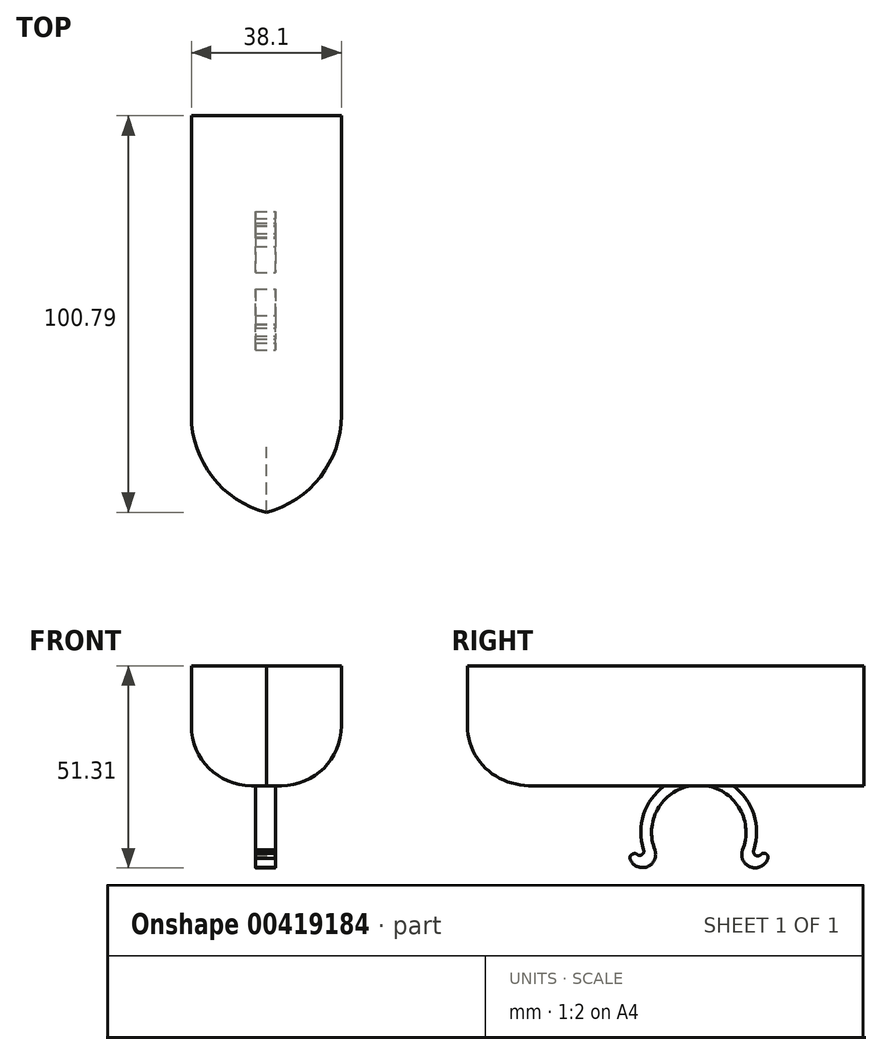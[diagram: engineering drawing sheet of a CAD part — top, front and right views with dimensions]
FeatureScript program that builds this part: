
annotation { "Feature Type Name" : "Feature", "Feature Type Description" : "" }
export const myFeature = defineFeature(function(context is Context, id is Id, definition is map)
    precondition{}
    {
        {
            var Q0;
            Q0=qCreatedBy(makeId("Top.planeOp"),FACE);
            var sketch = newSketch(context, id + "F0", { "sketchPlane" : qUnion([Q0])});
            skLineSegment(sketch, "E0.bottom", {"start": v(-26.44, 42) * mm, "end": v(11.66, 42) * mm});
            skLineSegment(sketch, "E0.top", {"start": v(-26.44, -59.6) * mm, "end": v(11.66, -59.6) * mm});
            skLineSegment(sketch, "E0.left", {"start": v(-26.44, 42) * mm, "end": v(-26.44, -59.6) * mm});
            skLineSegment(sketch, "E0.right", {"start": v(11.66, 42) * mm, "end": v(11.66, -59.6) * mm});
            skSolve(sketch);
        }
        {
            var Q0;
            Q0=makeQuery(id+"F0.imprint","IMPRINT",FACE,{"disambiguationData":[TD([[makeQuery(id+"F0.imprint","IMPRINT",EDGE,{"derivedFrom":sQuery(id+"F0.wireOp",EDGE,"E0.bottom")}),-1.0]])]});
            extrude(context, id + "F1", {"entities" : qUnion([Q0]), "depth" : 30.48 * mm});
        }
        {
            var Q0;
            Q0=makeQuery(id+"F1.opExtrude","SWEPT_EDGE",EDGE,{"disambiguationData":[OSD([sQuery(id+"F0.wireOp",EDGE,"E0.top"),sQuery(id+"F0.wireOp",EDGE,"E0.right")])]});
            var Q1;
            Q1=makeQuery(id+"F1.opExtrude","SWEPT_EDGE",EDGE,{"disambiguationData":[OSD([sQuery(id+"F0.wireOp",EDGE,"E0.top"),sQuery(id+"F0.wireOp",EDGE,"E0.left")])]});
            fillet(context, id + "F2", {"entities" : qUnion([Q0, Q1]), "radius" : 25.4 * mm, "tangentPropagation" : true, "allowEdgeOverflow" : false});
        }
        {
            var Q0;
            Q0=qCreatedBy(makeId("Right.planeOp"),FACE);
            cPlane(context, id + "F3", {"entities" : qUnion([Q0]), "cplaneType" : CPlaneType.OFFSET, "offset" : 5.08 * mm, "oppositeDirection" : true, "width" : 152.4 * mm, "height" : 152.4 * mm});
        }
        {
            var Q0;
            Q0=qCreatedBy(id+"F3.planeOp",FACE);
            var sketch = newSketch(context, id + "F4", { "sketchPlane" : qUnion([Q0])});
            skLineSegment(sketch, "E1", {"start": v(0, 0) * mm, "end": v(0, -52.03) * mm});
            skCircle(sketch, "E2", {"center": v(0, -11.8) * mm, "radius": 12 * mm});
            skCircle(sketch, "E3", {"center": v(0, -11.8) * mm, "radius": 14.7 * mm});
            skLineSegment(sketch, "E4", {"start": v(0, -18.44) * mm, "end": v(-17.52, -18.44) * mm});
            skLineSegment(sketch, "E5", {"start": v(0, -18.44) * mm, "end": v(17.53, -18.44) * mm});
            skLineSegment(sketch, "E6", {"start": v(0, -16.26) * mm, "end": v(-17.52, -16.26) * mm});
            skLineSegment(sketch, "E7", {"start": v(0, -16.26) * mm, "end": v(17.53, -16.26) * mm});
            skLineSegment(sketch, "E8", {"start": v(-17.52, -16.26) * mm, "end": v(-17.52, -18.44) * mm});
            skLineSegment(sketch, "E9", {"start": v(17.53, -16.26) * mm, "end": v(17.53, -18.44) * mm});
            skLineSegment(sketch, "E10", {"start": v(17.53, -17.35) * mm, "end": v(-17.52, -17.35) * mm});
            skPoint(sketch, "E11.endSnap0", {"position": v(-15.77, -17.32) * mm});
            skArc(sketch, "E12", {"start": v(-17.52, -18.44) * mm, "mid": v(-13.22, -20.6) * mm, "end": v(-11.13, -16.26) * mm});
            skArc(sketch, "E13", {"start": v(-15.77, -17.32) * mm, "mid": v(-14.46, -17.51) * mm, "end": v(-14.02, -16.26) * mm});
            skArc(sketch, "E14", {"start": v(11.13, -16.26) * mm, "mid": v(13.2, -20.65) * mm, "end": v(17.53, -18.44) * mm});
            skArc(sketch, "E15", {"start": v(-15.77, -17.32) * mm, "mid": v(-16.95, -17.4) * mm, "end": v(-17.52, -18.44) * mm});
            skArc(sketch, "E16", {"start": v(14.02, -16.26) * mm, "mid": v(14.45, -17.67) * mm, "end": v(15.88, -17.35) * mm});
            skArc(sketch, "E17", {"start": v(17.53, -18.44) * mm, "mid": v(17.12, -17.28) * mm, "end": v(15.88, -17.35) * mm});
            skSolve(sketch);
        }
        {
            var Q0;
            {var subQ0=sQuery(id+"F4.wireOp",EDGE,"E14");var subQ1=sQuery(id+"F4.wireOp",EDGE,"E3");var subQ2=makeQuery(id+"F4.imprint","INTERSECT",VERTEX,{"derivedFrom":[subQ1,subQ0]});Q0=makeQuery(id+"F4.imprint","IMPRINT",FACE,{"disambiguationData":[TD([[makeQuery(id+"F4.imprint","IMPRINT",EDGE,{"disambiguationData":[TD([[subQ2,-1.0]])],"derivedFrom":subQ1}),-1.0]])]});}
            var Q1;
            {var subQ6=sQuery(id+"F4.wireOp",EDGE,"E5");var subQ9=sQuery(id+"F4.wireOp",EDGE,"E3");var subQ10=makeQuery(id+"F4.imprint","INTERSECT",VERTEX,{"derivedFrom":[subQ9,subQ6]});Q1=makeQuery(id+"F4.imprint","IMPRINT",FACE,{"disambiguationData":[TD([[makeQuery(id+"F4.imprint","IMPRINT",EDGE,{"disambiguationData":[TD([[subQ10,-1.0]])],"derivedFrom":subQ9}),-1.0]])]});}
            var Q2;
            {var subQ0=sQuery(id+"F4.wireOp",EDGE,"E17");var subQ1=sQuery(id+"F4.wireOp",EDGE,"E10");var subQ3=makeQuery(id+"F4.imprint","INTERSECT",VERTEX,{"derivedFrom":[subQ1,subQ0]});Q2=makeQuery(id+"F4.imprint","IMPRINT",FACE,{"disambiguationData":[TD([[makeQuery(id+"F4.imprint","IMPRINT",EDGE,{"disambiguationData":[TD([[subQ3,-1.0]])],"derivedFrom":subQ1}),-1.0]])]});}
            var Q3;
            {var subQ0=sQuery(id+"F4.wireOp",EDGE,"E17");var subQ1=sQuery(id+"F4.wireOp",EDGE,"E9");var subQ3=makeQuery(id+"F4.imprint","INTERSECT",VERTEX,{"derivedFrom":[subQ1,subQ0]});Q3=makeQuery(id+"F4.imprint","IMPRINT",FACE,{"disambiguationData":[TD([[makeQuery(id+"F4.imprint","IMPRINT",EDGE,{"disambiguationData":[TD([[subQ3,-1.0]])],"derivedFrom":subQ1}),1.0]])]});}
            var Q4;
            {var subQ0=sQuery(id+"F4.wireOp",EDGE,"E10");var subQ1=sQuery(id+"F4.wireOp",EDGE,"E3");var subQ2=makeQuery(id+"F4.imprint","INTERSECT",VERTEX,{"disambiguationData":[OD(1.0)],"derivedFrom":[subQ1,subQ0]});Q4=makeQuery(id+"F4.imprint","IMPRINT",FACE,{"disambiguationData":[TD([[makeQuery(id+"F4.imprint","IMPRINT",EDGE,{"disambiguationData":[TD([[subQ2,-1.0]])],"derivedFrom":subQ1}),-1.0]])]});}
            var Q5;
            {var subQ3=sQuery(id+"F4.wireOp",EDGE,"E10");var subQ5=sQuery(id+"F4.wireOp",EDGE,"E3");var subQ6=makeQuery(id+"F4.imprint","INTERSECT",VERTEX,{"disambiguationData":[OD(1.0)],"derivedFrom":[subQ5,subQ3]});Q5=makeQuery(id+"F4.imprint","IMPRINT",FACE,{"disambiguationData":[TD([[makeQuery(id+"F4.imprint","IMPRINT",EDGE,{"disambiguationData":[TD([[subQ6,-1.0]])],"derivedFrom":subQ5}),1.0]])]});}
            var Q6;
            {var subQ0=sQuery(id+"F4.wireOp",EDGE,"E5");var subQ1=sQuery(id+"F4.wireOp",EDGE,"E3");var subQ2=makeQuery(id+"F4.imprint","INTERSECT",VERTEX,{"derivedFrom":[subQ1,subQ0]});Q6=makeQuery(id+"F4.imprint","IMPRINT",FACE,{"disambiguationData":[TD([[makeQuery(id+"F4.imprint","IMPRINT",EDGE,{"disambiguationData":[TD([[subQ2,-1.0]])],"derivedFrom":subQ1}),1.0]])]});}
            var Q7;
            {var subQ0=sQuery(id+"F4.wireOp",EDGE,"E14");var subQ1=sQuery(id+"F4.wireOp",EDGE,"E3");var subQ2=makeQuery(id+"F4.imprint","INTERSECT",VERTEX,{"derivedFrom":[subQ1,subQ0]});Q7=makeQuery(id+"F4.imprint","IMPRINT",FACE,{"disambiguationData":[TD([[makeQuery(id+"F4.imprint","IMPRINT",EDGE,{"disambiguationData":[TD([[subQ2,-1.0]])],"derivedFrom":subQ1}),1.0]])]});}
            var Q8;
            {var subQ0=sQuery(id+"F4.wireOp",EDGE,"E6");var subQ1=sQuery(id+"F4.wireOp",EDGE,"E2");var subQ2=makeQuery(id+"F4.imprint","INTERSECT",VERTEX,{"derivedFrom":[subQ1,subQ0,sQuery(id+"F4.wireOp",EDGE,"E12")]});Q8=makeQuery(id+"F4.imprint","IMPRINT",FACE,{"disambiguationData":[TD([[makeQuery(id+"F4.imprint","IMPRINT",EDGE,{"disambiguationData":[TD([[subQ2,1.0]])],"derivedFrom":subQ1}),-1.0]])]});}
            var Q9;
            {var subQ5=sQuery(id+"F4.wireOp",EDGE,"E3");var subQ7=sQuery(id+"F4.wireOp",EDGE,"E13");var subQ9=makeQuery(id+"F4.imprint","INTERSECT",VERTEX,{"derivedFrom":[subQ5,subQ7]});Q9=makeQuery(id+"F4.imprint","IMPRINT",FACE,{"disambiguationData":[TD([[makeQuery(id+"F4.imprint","IMPRINT",EDGE,{"disambiguationData":[TD([[subQ9,-1.0]])],"derivedFrom":subQ5}),1.0]])]});}
            var Q10;
            {var subQ0=sQuery(id+"F4.wireOp",EDGE,"E10");var subQ1=sQuery(id+"F4.wireOp",EDGE,"E3");var subQ2=makeQuery(id+"F4.imprint","INTERSECT",VERTEX,{"disambiguationData":[OD(0.0)],"derivedFrom":[subQ1,subQ0]});Q10=makeQuery(id+"F4.imprint","IMPRINT",FACE,{"disambiguationData":[TD([[makeQuery(id+"F4.imprint","IMPRINT",EDGE,{"disambiguationData":[TD([[subQ2,-1.0]])],"derivedFrom":subQ1}),1.0]])]});}
            var Q11;
            {var subQ0=sQuery(id+"F4.wireOp",EDGE,"E12");var subQ1=sQuery(id+"F4.wireOp",EDGE,"E3");var subQ2=makeQuery(id+"F4.imprint","INTERSECT",VERTEX,{"derivedFrom":[subQ1,subQ0]});Q11=makeQuery(id+"F4.imprint","IMPRINT",FACE,{"disambiguationData":[TD([[makeQuery(id+"F4.imprint","IMPRINT",EDGE,{"disambiguationData":[TD([[subQ2,1.0]])],"derivedFrom":subQ1}),1.0]])]});}
            var Q12;
            {var subQ0=sQuery(id+"F4.wireOp",EDGE,"E12");var subQ1=sQuery(id+"F4.wireOp",EDGE,"E3");var subQ2=makeQuery(id+"F4.imprint","INTERSECT",VERTEX,{"derivedFrom":[subQ1,subQ0]});Q12=makeQuery(id+"F4.imprint","IMPRINT",FACE,{"disambiguationData":[TD([[makeQuery(id+"F4.imprint","IMPRINT",EDGE,{"disambiguationData":[TD([[subQ2,1.0]])],"derivedFrom":subQ1}),-1.0]])]});}
            var Q13;
            {var subQ0=sQuery(id+"F4.wireOp",EDGE,"E10");var subQ1=sQuery(id+"F4.wireOp",EDGE,"E3");var subQ2=makeQuery(id+"F4.imprint","INTERSECT",VERTEX,{"disambiguationData":[OD(0.0)],"derivedFrom":[subQ1,subQ0]});Q13=makeQuery(id+"F4.imprint","IMPRINT",FACE,{"disambiguationData":[TD([[makeQuery(id+"F4.imprint","IMPRINT",EDGE,{"disambiguationData":[TD([[subQ2,-1.0]])],"derivedFrom":subQ1}),-1.0]])]});}
            var Q14;
            {var subQ0=sQuery(id+"F4.wireOp",EDGE,"E13");var subQ1=sQuery(id+"F4.wireOp",EDGE,"E10");var subQ2=makeQuery(id+"F4.imprint","INTERSECT",VERTEX,{"disambiguationData":[OD(1.0)],"derivedFrom":[subQ1,subQ0]});Q14=makeQuery(id+"F4.imprint","IMPRINT",FACE,{"disambiguationData":[TD([[makeQuery(id+"F4.imprint","IMPRINT",EDGE,{"disambiguationData":[TD([[subQ2,-1.0]])],"derivedFrom":subQ1}),-1.0]])]});}
            var Q15;
            {var subQ0=sQuery(id+"F4.wireOp",EDGE,"E13");var subQ1=sQuery(id+"F4.wireOp",EDGE,"E3");var subQ2=makeQuery(id+"F4.imprint","INTERSECT",VERTEX,{"derivedFrom":[subQ1,subQ0]});Q15=makeQuery(id+"F4.imprint","IMPRINT",FACE,{"disambiguationData":[TD([[makeQuery(id+"F4.imprint","IMPRINT",EDGE,{"disambiguationData":[TD([[subQ2,-1.0]])],"derivedFrom":subQ1}),-1.0]])]});}
            extrude(context, id + "F5", {"entities" : qUnion([Q0, Q1, Q2, Q3, Q4, Q5, Q6, Q7, Q8, Q9, Q10, Q11, Q12, Q13, Q14, Q15]), "operationType" : NewBodyOperationType.ADD, "oppositeDirection" : true, "depth" : 5.08 * mm});
        }
        {
            var Q0;
            {var subQ0=sQuery(id+"F0.wireOp",EDGE,"E0.right");var subQ1=sQuery(id+"F0.wireOp",EDGE,"E0.top");Q0=makeQuery(id+"F2.opFillet","BLEND_EDGE",EDGE,{"blendedFrom":[makeQuery(id+"F1.opExtrude","SWEPT_EDGE",EDGE,{"disambiguationData":[OSD([subQ1,subQ0])]}),makeQuery(id+"F1.opExtrude","CAP_FACE",FACE,{"disambiguationData":[OSD([sQuery(id+"F0.wireOp",EDGE,"E0.bottom"),subQ1,sQuery(id+"F0.wireOp",EDGE,"E0.left"),subQ0])],"isStart":true})],"blendedInto":[makeQuery(id+"F1.opExtrude","CAP_FACE",FACE,{"disambiguationData":[OSD([sQuery(id+"F0.wireOp",EDGE,"E0.bottom"),subQ1,sQuery(id+"F0.wireOp",EDGE,"E0.left"),subQ0])],"isStart":true})]});}
            var Q1;
            {var subQ0=sQuery(id+"F0.wireOp",EDGE,"E0.left");var subQ1=sQuery(id+"F0.wireOp",EDGE,"E0.top");Q1=makeQuery(id+"F2.opFillet","BLEND_EDGE",EDGE,{"blendedFrom":[makeQuery(id+"F1.opExtrude","SWEPT_EDGE",EDGE,{"disambiguationData":[OSD([subQ1,subQ0])]}),makeQuery(id+"F1.opExtrude","CAP_FACE",FACE,{"disambiguationData":[OSD([sQuery(id+"F0.wireOp",EDGE,"E0.bottom"),subQ1,subQ0,sQuery(id+"F0.wireOp",EDGE,"E0.right")])],"isStart":true})],"blendedInto":[makeQuery(id+"F1.opExtrude","CAP_FACE",FACE,{"disambiguationData":[OSD([sQuery(id+"F0.wireOp",EDGE,"E0.bottom"),subQ1,subQ0,sQuery(id+"F0.wireOp",EDGE,"E0.right")])],"isStart":true})]});}
            fillet(context, id + "F6", {"entities" : qUnion([Q0, Q1]), "radius" : 15.24 * mm, "tangentPropagation" : true, "allowEdgeOverflow" : false});
        }
    });
